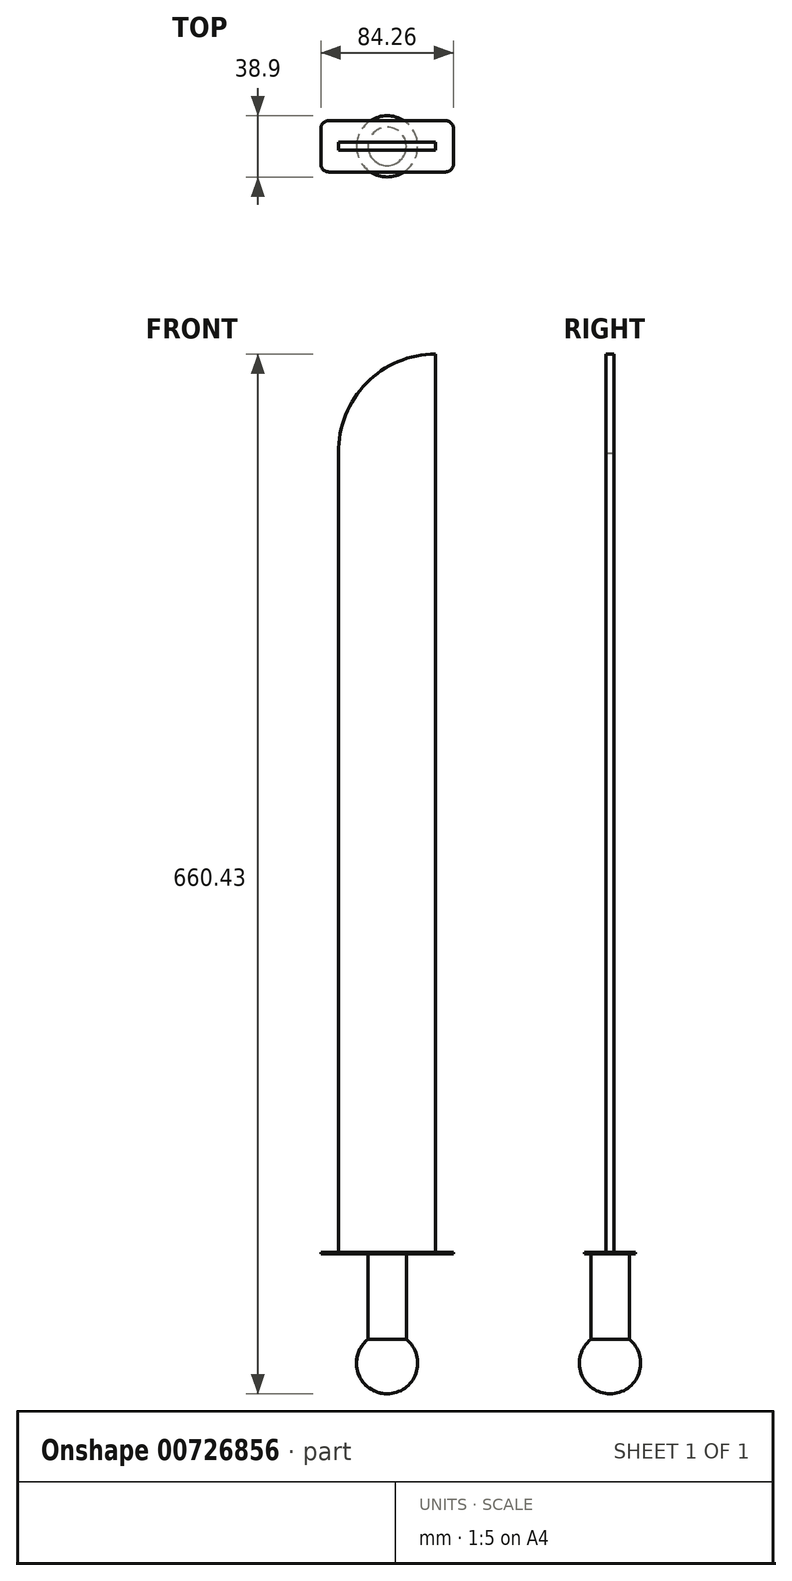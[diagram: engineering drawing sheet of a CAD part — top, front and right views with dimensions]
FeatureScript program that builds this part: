
annotation { "Feature Type Name" : "Feature", "Feature Type Description" : "" }
export const myFeature = defineFeature(function(context is Context, id is Id, definition is map)
    precondition{}
    {
        {
            var Q0;
            Q0=qCreatedBy(makeId("Top.planeOp"),FACE);
            var sketch = newSketch(context, id + "F0", { "sketchPlane" : qUnion([Q0])});
            skLineSegment(sketch, "E0.bottom", {"start": v(42.13, 16.26) * mm, "end": v(-42.13, 16.26) * mm});
            skLineSegment(sketch, "E0.top", {"start": v(42.13, -16.26) * mm, "end": v(-42.13, -16.26) * mm});
            skLineSegment(sketch, "E0.left", {"start": v(42.13, 16.26) * mm, "end": v(42.13, -16.26) * mm});
            skLineSegment(sketch, "E0.right", {"start": v(-42.13, 16.26) * mm, "end": v(-42.13, -16.26) * mm});
            skPoint(sketch, "E0.middle", {"position": v(0, 0) * mm});
            skSolve(sketch);
        }
        {
            var Q0;
            Q0 = qSketchRegion(id + "F0", true);
            extrude(context, id + "F1", {"entities" : qUnion([Q0]), "endBound" : BoundingType.SYMMETRIC, "depth" : 1 * mm, "offsetDistance" : 25.4 * mm});
        }
        {
            var Q0;
            Q0=qCreatedBy(makeId("Front.planeOp"),FACE);
            var sketch = newSketch(context, id + "F2", { "sketchPlane" : qUnion([Q0])});
            skLineSegment(sketch, "E1.bottom", {"start": v(-12.2, 0) * mm, "end": v(0, 0) * mm});
            skLineSegment(sketch, "E1.left", {"start": v(-12.2, 0) * mm, "end": v(-12.2, -54.7) * mm});
            skPoint(sketch, "E1.middle", {"position": v(0, -27.35) * mm});
            skArc(sketch, "E2", {"start": v(-12.2, -54.7) * mm, "mid": v(-18.34, -76.31) * mm, "end": v(0, -89.3) * mm});
            skPoint(sketch, "E2.centerSnap0", {"position": v(0, -54.7) * mm});
            skLineSegment(sketch, "E3", {"start": v(0, 0) * mm, "end": v(0, -89.3) * mm});
            skPoint(sketch, "E1.right.end.orphan", {"position": v(12.2, -54.7) * mm});
            skPoint(sketch, "E4.orphan", {"position": v(12.2, 0) * mm});
            skSolve(sketch);
        }
        {
            var Q0;
            Q0=makeQuery(id+"F2.imprint","IMPRINT",FACE,{"disambiguationData":[TD([[makeQuery(id+"F2.imprint","IMPRINT",EDGE,{"derivedFrom":sQuery(id+"F2.wireOp",EDGE,"E1.bottom")}),-1.0]])]});
            var Q1;
            Q1=sQuery(id+"F2.wireOp",EDGE,"E3");
            var Q2;
            Q2=sQuery(id+"F2.wireOp",EDGE,"E1.left");
            var Q3;
            Q3=sQuery(id+"F2.wireOp",EDGE,"E2");
            var Q4;
            Q4=sQuery(id+"F2.wireOp",EDGE,"E1.bottom");
            var Q5;
            Q5=sQuery(id+"F2.wireOp",EDGE,"E3");
            revolve(context, id + "F3", {"operationType" : NewBodyOperationType.ADD, "surfaceOperationType" : NewSurfaceOperationType.NEW, "entities" : qUnion([Q0]), "surfaceEntities" : qUnion([Q1, Q2, Q3, Q4]), "axis" : qUnion([Q5]), "revolveType" : RevolveType.FULL});
        }
        {
            var Q0;
            Q0=qCreatedBy(makeId("Front.planeOp"),FACE);
            var sketch = newSketch(context, id + "F4", { "sketchPlane" : qUnion([Q0])});
            skLineSegment(sketch, "E5.bottom", {"start": v(-30.75, 0) * mm, "end": v(30.75, 0) * mm});
            skLineSegment(sketch, "E5.left", {"start": v(-30.75, 0) * mm, "end": v(-30.75, 510.87) * mm});
            skLineSegment(sketch, "E5.right", {"start": v(30.75, 0) * mm, "end": v(30.75, 571.14) * mm});
            skPoint(sketch, "E5.middle", {"position": v(0, 285.57) * mm});
            skArc(sketch, "E6", {"start": v(30.75, 571.14) * mm, "mid": v(-13.18, 552.69) * mm, "end": v(-30.75, 508.39) * mm});
            skPoint(sketch, "E7.orphan", {"position": v(-30.75, 571.14) * mm});
            skSolve(sketch);
        }
        {
            var Q0;
            Q0 = qSketchRegion(id + "F4", true);
            extrude(context, id + "F5", {"entities" : qUnion([Q0]), "operationType" : NewBodyOperationType.ADD, "endBound" : BoundingType.SYMMETRIC, "depth" : 5 * mm, "offsetDistance" : 25.4 * mm});
        }
        {
            var Q0;
            Q0=makeQuery(id+"F1.opExtrude","SWEPT_EDGE",EDGE,{"disambiguationData":[OSD([sQuery(id+"F0.wireOp",EDGE,"E0.top"),sQuery(id+"F0.wireOp",EDGE,"E0.right")])]});
            var Q1;
            Q1=makeQuery(id+"F1.opExtrude","SWEPT_EDGE",EDGE,{"disambiguationData":[OSD([sQuery(id+"F0.wireOp",EDGE,"E0.bottom"),sQuery(id+"F0.wireOp",EDGE,"E0.right")])]});
            var Q2;
            Q2=makeQuery(id+"F1.opExtrude","SWEPT_EDGE",EDGE,{"disambiguationData":[OSD([sQuery(id+"F0.wireOp",EDGE,"E0.bottom"),sQuery(id+"F0.wireOp",EDGE,"E0.left")])]});
            var Q3;
            Q3=makeQuery(id+"F1.opExtrude","SWEPT_EDGE",EDGE,{"disambiguationData":[OSD([sQuery(id+"F0.wireOp",EDGE,"E0.top"),sQuery(id+"F0.wireOp",EDGE,"E0.left")])]});
            fillet(context, id + "F6", {"entities" : qUnion([Q0, Q1, Q2, Q3]), "radius" : 5.08 * mm, "tangentPropagation" : true, "allowEdgeOverflow" : false});
        }
    });
